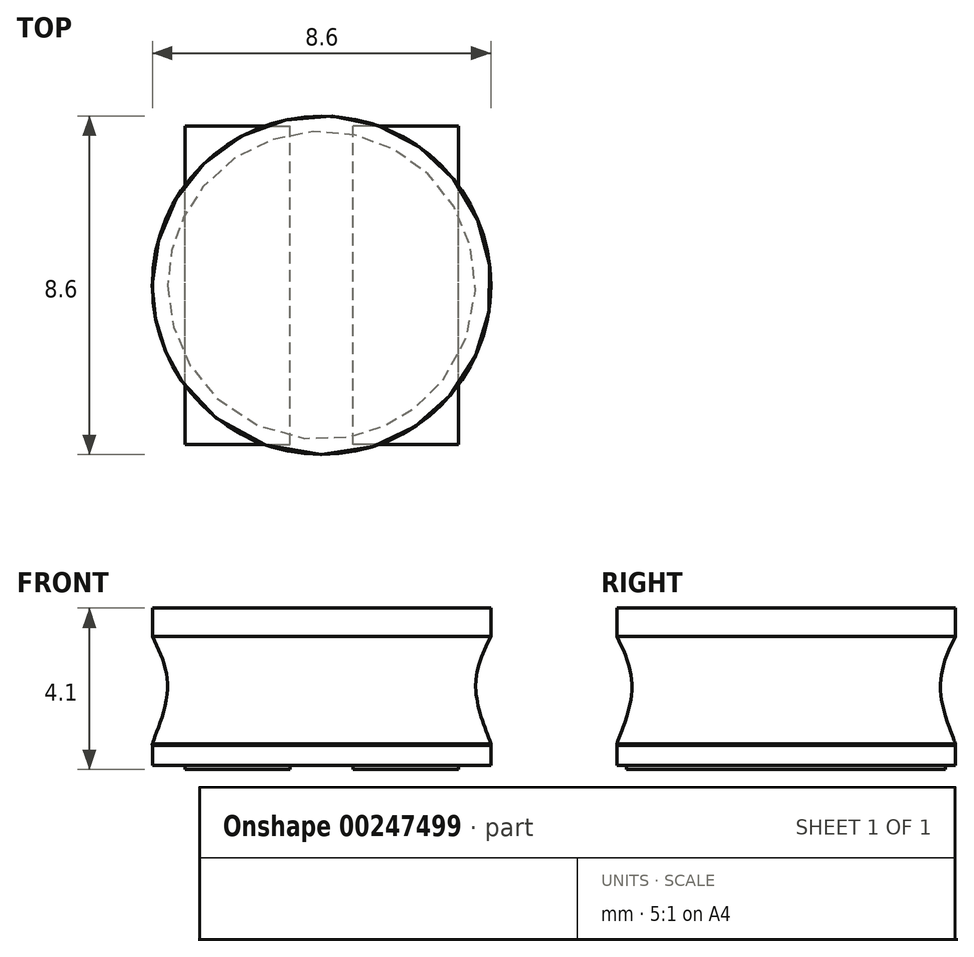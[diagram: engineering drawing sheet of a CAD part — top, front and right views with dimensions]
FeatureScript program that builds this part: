
annotation { "Feature Type Name" : "Feature", "Feature Type Description" : "" }
export const myFeature = defineFeature(function(context is Context, id is Id, definition is map)
    precondition{}
    {
        {
            var Q0;
            Q0=qCreatedBy(makeId("Front.planeOp"),FACE);
            var sketch = newSketch(context, id + "F0", { "sketchPlane" : qUnion([Q0])});
            skLineSegment(sketch, "E0.bottom", {"start": v(0, 0) * mm, "end": v(4.3, 0) * mm});
            skLineSegment(sketch, "E0.top", {"start": v(0, 4) * mm, "end": v(4.3, 4) * mm});
            skLineSegment(sketch, "E0.left", {"start": v(0, 0) * mm, "end": v(0, 4) * mm});
            skLineSegment(sketch, "E0.right", {"start": v(4.3, 0) * mm, "end": v(4.3, 0.55) * mm});
            skFitSpline(sketch, "E1", {"points": [v(4.3, 3.28) * mm, v(3.92, 1.82) * mm, v(4.3, 0.55) * mm, v(4.3, 0.51) * mm], "startDerivative": vector(-1.36, -2.84) * mm, "endDerivative": vector(-0.1, -0.3) * mm});
            skLineSegment(sketch, "E2.trimOffspring", {"start": v(4.3, 3.28) * mm, "end": v(4.3, 4) * mm});
            skSolve(sketch);
        }
        {
            var Q0;
            Q0=qSketchRegion(id+"F0",true);
            var Q1;
            Q1=sQuery(id+"F0.wireOp",EDGE,"E0.left");
            revolve(context, id + "F1", {"entities" : qUnion([Q0]), "axis" : qUnion([Q1]), "revolveType" : RevolveType.FULL});
        }
        {
            var Q0;
            Q0=makeQuery(id+"F1.opRevolve","SWEPT_FACE",FACE,{"disambiguationData":[OSD([sQuery(id+"F0.wireOp",EDGE,"E0.bottom")])]});
            var sketch = newSketch(context, id + "F2", { "sketchPlane" : qUnion([Q0])});
            skLineSegment(sketch, "E3", {"start": v(-8.59, 0) * mm, "end": v(9.64, 0) * mm, "construction": true});
            skLineSegment(sketch, "E4", {"start": v(0, 6.6) * mm, "end": v(0, -6.85) * mm, "construction": true});
            skLineSegment(sketch, "E5.bottom", {"start": v(3.48, 4.05) * mm, "end": v(0.8, 4.05) * mm});
            skLineSegment(sketch, "E5.top", {"start": v(3.48, -4.05) * mm, "end": v(0.8, -4.05) * mm});
            skLineSegment(sketch, "E5.left", {"start": v(3.48, 4.05) * mm, "end": v(3.48, -4.05) * mm});
            skLineSegment(sketch, "E5.right", {"start": v(0.8, 4.05) * mm, "end": v(0.8, -4.05) * mm});
            skPoint(sketch, "E5.middle", {"position": v(2.14, 0) * mm});
            skLineSegment(sketch, "E6.MirrorCS", {"start": v(-0.8, 4.05) * mm, "end": v(-0.8, -4.05) * mm});
            skLineSegment(sketch, "E7.MirrorCS", {"start": v(-3.48, 4.05) * mm, "end": v(-3.48, -4.05) * mm});
            skLineSegment(sketch, "E8.MirrorCS", {"start": v(-3.48, -4.05) * mm, "end": v(-0.8, -4.05) * mm});
            skPoint(sketch, "E9.MirrorP", {"position": v(-2.14, 0) * mm});
            skLineSegment(sketch, "E10.MirrorCS", {"start": v(8.59, 0) * mm, "end": v(-9.64, 0) * mm, "construction": true});
            skLineSegment(sketch, "E11.MirrorCS", {"start": v(-3.48, 4.05) * mm, "end": v(-0.8, 4.05) * mm});
            skSolve(sketch);
        }
        {
            var Q0;
            Q0=qSketchRegion(id+"F2",true);
            extrude(context, id + "F3", {"entities" : qUnion([Q0]), "depth" : .1 * mm});
        }
    });
